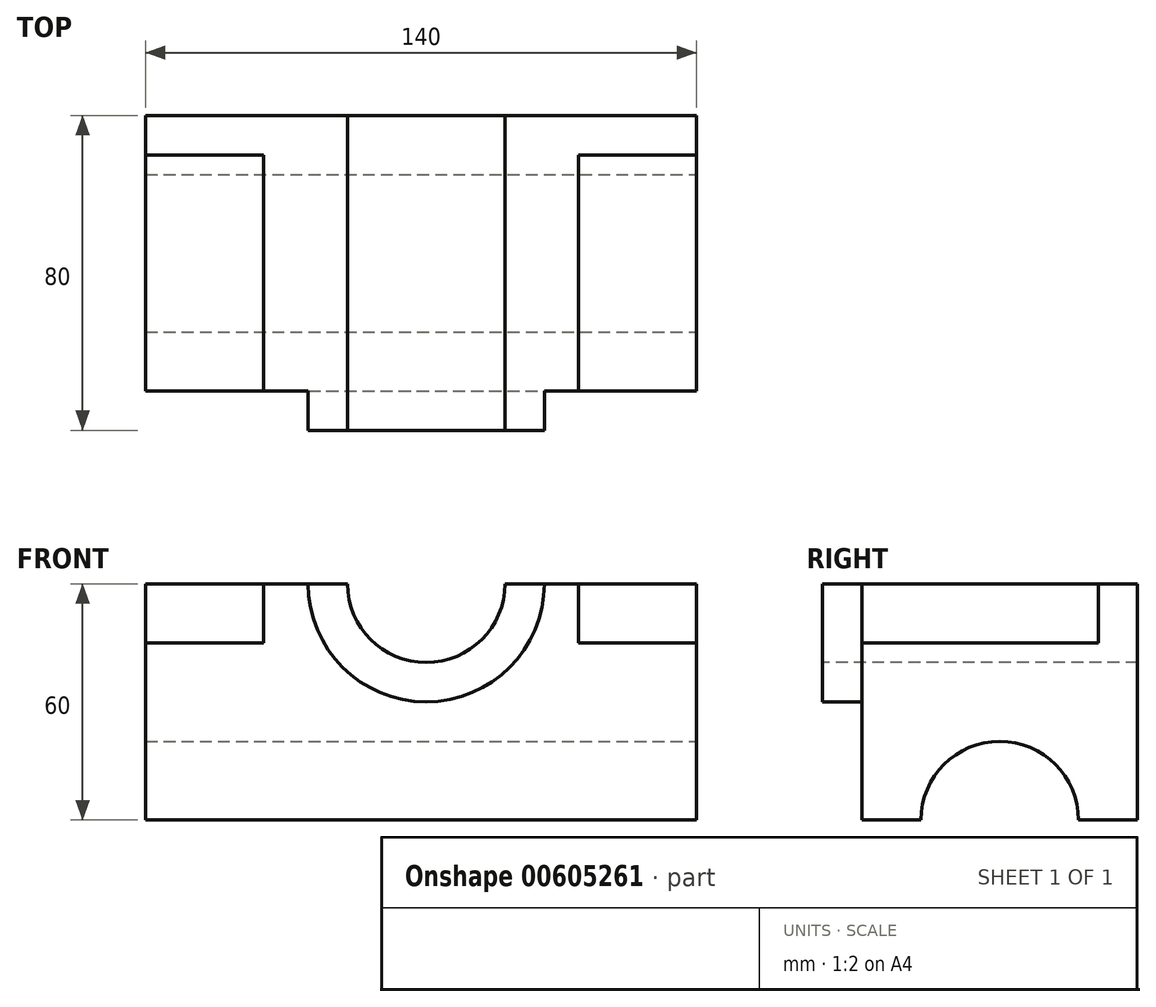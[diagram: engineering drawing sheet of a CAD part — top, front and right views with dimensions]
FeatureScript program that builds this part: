
annotation { "Feature Type Name" : "Feature", "Feature Type Description" : "" }
export const myFeature = defineFeature(function(context is Context, id is Id, definition is map)
    precondition{}
    {
        {
            var Q0;
            Q0=qCreatedBy(makeId("Top.planeOp"),FACE);
            var sketch = newSketch(context, id + "F0", { "sketchPlane" : qUnion([Q0])});
            skLineSegment(sketch, "E0.bottom", {"start": v(-71.28, 46.73) * mm, "end": v(68.72, 46.73) * mm});
            skLineSegment(sketch, "E0.top", {"start": v(-71.28, -23.27) * mm, "end": v(68.72, -23.27) * mm});
            skLineSegment(sketch, "E0.left", {"start": v(-71.28, 46.73) * mm, "end": v(-71.28, -23.27) * mm});
            skLineSegment(sketch, "E0.right", {"start": v(68.72, 46.73) * mm, "end": v(68.72, -23.27) * mm});
            skSolve(sketch);
        }
        {
            var Q0;
            Q0=makeQuery(id+"F0.imprint","IMPRINT",FACE,{"disambiguationData":[TD([[makeQuery(id+"F0.imprint","IMPRINT",EDGE,{"derivedFrom":sQuery(id+"F0.wireOp",EDGE,"E0.bottom")}),-1.0]])]});
            extrude(context, id + "F1", {"entities" : qUnion([Q0]), "depth" : 60 * mm, "offsetDistance" : 25 * mm});
        }
        {
            var Q0;
            Q0=makeQuery(id+"F1.opExtrude","SWEPT_FACE",FACE,{"disambiguationData":[OSD([sQuery(id+"F0.wireOp",EDGE,"E0.right")])]});
            var sketch = newSketch(context, id + "F2", { "sketchPlane" : qUnion([Q0])});
            skCircle(sketch, "E1", {"center": v(11.73, 0) * mm, "radius": 20 * mm});
            skSolve(sketch);
        }
        {
            var Q0;
            {var subQ0=sQuery(id+"F2.wireOp",EDGE,"E1");var subQ1=makeQuery(id+"F1.opExtrude","CAP_EDGE",EDGE,{"disambiguationData":[OSD([sQuery(id+"F0.wireOp",EDGE,"E0.right")])],"isStart":true});var subQ2=makeQuery(id+"F2.imprint","INTERSECT",VERTEX,{"disambiguationData":[OD(0.0)],"derivedFrom":[subQ1,subQ0]});Q0=makeQuery(id+"F2.imprint","IMPRINT",FACE,{"disambiguationData":[TD([[makeQuery(id+"F2.imprint","IMPRINT",EDGE,{"disambiguationData":[TD([[subQ2,-1.0]])],"derivedFrom":subQ0}),1.0]])]});}
            extrude(context, id + "F3", {"entities" : qUnion([Q0]), "operationType" : NewBodyOperationType.REMOVE, "oppositeDirection" : true, "depth" : 140 * mm, "offsetDistance" : 25 * mm});
        }
        {
            var Q0;
            Q0=makeQuery(id+"F1.opExtrude","SWEPT_FACE",FACE,{"disambiguationData":[OSD([sQuery(id+"F0.wireOp",EDGE,"E0.top")])]});
            var sketch = newSketch(context, id + "F4", { "sketchPlane" : qUnion([Q0])});
            skCircle(sketch, "E2", {"center": v(0, 60) * mm, "radius": 20 * mm});
            skCircle(sketch, "E3", {"center": v(0, 60) * mm, "radius": 30 * mm});
            skSolve(sketch);
        }
        {
            var Q0;
            {var subQ0=sQuery(id+"F4.wireOp",EDGE,"E2");var subQ1=makeQuery(id+"F1.opExtrude","CAP_EDGE",EDGE,{"disambiguationData":[OSD([sQuery(id+"F0.wireOp",EDGE,"E0.top")])],"isStart":false});var subQ2=makeQuery(id+"F4.imprint","INTERSECT",VERTEX,{"disambiguationData":[OD(0.0)],"derivedFrom":[subQ1,subQ0]});Q0=makeQuery(id+"F4.imprint","IMPRINT",FACE,{"disambiguationData":[TD([[makeQuery(id+"F4.imprint","IMPRINT",EDGE,{"disambiguationData":[TD([[subQ2,-1.0]])],"derivedFrom":subQ0}),1.0]])]});}
            extrude(context, id + "F5", {"entities" : qUnion([Q0]), "operationType" : NewBodyOperationType.REMOVE, "oppositeDirection" : true, "depth" : 70 * mm, "offsetDistance" : 25 * mm});
        }
        {
            var Q0;
            {var subQ0=sQuery(id+"F4.wireOp",EDGE,"E2");var subQ1=makeQuery(id+"F1.opExtrude","CAP_EDGE",EDGE,{"disambiguationData":[OSD([sQuery(id+"F0.wireOp",EDGE,"E0.top")])],"isStart":false});var subQ2=makeQuery(id+"F4.imprint","INTERSECT",VERTEX,{"disambiguationData":[OD(0.0)],"derivedFrom":[subQ1,subQ0]});Q0=makeQuery(id+"F4.imprint","IMPRINT",FACE,{"disambiguationData":[TD([[makeQuery(id+"F4.imprint","IMPRINT",EDGE,{"disambiguationData":[TD([[subQ2,-1.0]])],"derivedFrom":subQ0}),-1.0]])]});}
            extrude(context, id + "F6", {"entities" : qUnion([Q0]), "operationType" : NewBodyOperationType.ADD, "depth" : 10 * mm, "offsetDistance" : 25 * mm});
        }
        {
            var Q0;
            {var subQ0=sQuery(id+"F0.wireOp",EDGE,"E0.top");var subQ1=makeQuery(id+"F1.opExtrude","CAP_EDGE",EDGE,{"disambiguationData":[OSD([subQ0])],"isStart":false});var subQ3=sQuery(id+"F0.wireOp",EDGE,"E0.bottom");var subQ4=sQuery(id+"F0.wireOp",EDGE,"E0.left");Q0=makeQuery(id+"F6.boolean.opBoolean","MERGE",FACE,{"derivedFrom":[makeQuery(id+"F5.boolean.opBoolean","SPLIT",FACE,{"disambiguationData":[TD([makeQuery(id+"F1.opExtrude","SWEPT_FACE",FACE,{"disambiguationData":[OSD([subQ4])]})])],"derivedFrom":makeQuery(id+"F1.opExtrude","CAP_FACE",FACE,{"disambiguationData":[OSD([subQ3,subQ0,subQ4,sQuery(id+"F0.wireOp",EDGE,"E0.right")])],"isStart":false})}),makeQuery(id+"F6.opExtrude","SWEPT_FACE",FACE,{"disambiguationData":[OSD([subQ0]),TDD([makeQuery(id+"F4.imprint","IMPRINT",EDGE,{"disambiguationData":[TD([[makeQuery(id+"F4.imprint","INTERSECT",VERTEX,{"disambiguationData":[OD(0.0)],"derivedFrom":[subQ1,sQuery(id+"F4.wireOp",EDGE,"E3")]}),-1.0]])],"derivedFrom":subQ1})])]})]});}
            var sketch = newSketch(context, id + "F7", { "sketchPlane" : qUnion([Q0])});
            skLineSegment(sketch, "E4.bottom", {"start": v(-71.28, -23.27) * mm, "end": v(-41.28, -23.27) * mm});
            skLineSegment(sketch, "E4.top", {"start": v(-71.28, 36.73) * mm, "end": v(-41.28, 36.73) * mm});
            skLineSegment(sketch, "E4.left", {"start": v(-71.28, -23.27) * mm, "end": v(-71.28, 36.73) * mm});
            skLineSegment(sketch, "E4.right", {"start": v(-41.28, -23.27) * mm, "end": v(-41.28, 36.73) * mm});
            skSolve(sketch);
        }
        {
            var Q0;
            Q0=makeQuery(id+"F7.imprint","IMPRINT",FACE,{"disambiguationData":[TD([[makeQuery(id+"F7.imprint","IMPRINT",EDGE,{"derivedFrom":sQuery(id+"F7.wireOp",EDGE,"E4.bottom")}),1.0]])]});
            extrude(context, id + "F8", {"entities" : qUnion([Q0]), "operationType" : NewBodyOperationType.REMOVE, "oppositeDirection" : true, "depth" : 15 * mm, "offsetDistance" : 25 * mm});
        }
        {
            var Q0;
            {var subQ0=sQuery(id+"F0.wireOp",EDGE,"E0.top");var subQ1=makeQuery(id+"F1.opExtrude","CAP_EDGE",EDGE,{"disambiguationData":[OSD([subQ0])],"isStart":false});var subQ3=sQuery(id+"F0.wireOp",EDGE,"E0.bottom");var subQ4=sQuery(id+"F0.wireOp",EDGE,"E0.right");Q0=makeQuery(id+"F6.boolean.opBoolean","MERGE",FACE,{"derivedFrom":[makeQuery(id+"F5.boolean.opBoolean","SPLIT",FACE,{"disambiguationData":[TD([makeQuery(id+"F1.opExtrude","SWEPT_FACE",FACE,{"disambiguationData":[OSD([subQ4])]})])],"derivedFrom":makeQuery(id+"F1.opExtrude","CAP_FACE",FACE,{"disambiguationData":[OSD([subQ3,subQ0,sQuery(id+"F0.wireOp",EDGE,"E0.left"),subQ4])],"isStart":false})}),makeQuery(id+"F6.opExtrude","SWEPT_FACE",FACE,{"disambiguationData":[OSD([subQ0]),TDD([makeQuery(id+"F4.imprint","IMPRINT",EDGE,{"disambiguationData":[TD([[makeQuery(id+"F4.imprint","INTERSECT",VERTEX,{"disambiguationData":[OD(1.0)],"derivedFrom":[subQ1,sQuery(id+"F4.wireOp",EDGE,"E3")]}),1.0]])],"derivedFrom":subQ1})])]})]});}
            var sketch = newSketch(context, id + "F9", { "sketchPlane" : qUnion([Q0])});
            skLineSegment(sketch, "E5.bottom", {"start": v(68.72, -23.27) * mm, "end": v(38.72, -23.27) * mm});
            skLineSegment(sketch, "E5.top", {"start": v(68.72, 36.73) * mm, "end": v(38.72, 36.73) * mm});
            skLineSegment(sketch, "E5.left", {"start": v(68.72, -23.27) * mm, "end": v(68.72, 36.73) * mm});
            skLineSegment(sketch, "E5.right", {"start": v(38.72, -23.27) * mm, "end": v(38.72, 36.73) * mm});
            skSolve(sketch);
        }
        {
            var Q0;
            Q0=makeQuery(id+"F9.imprint","IMPRINT",FACE,{"disambiguationData":[TD([[makeQuery(id+"F9.imprint","IMPRINT",EDGE,{"derivedFrom":sQuery(id+"F9.wireOp",EDGE,"E5.bottom")}),1.0]])]});
            extrude(context, id + "F10", {"entities" : qUnion([Q0]), "operationType" : NewBodyOperationType.REMOVE, "oppositeDirection" : true, "depth" : 15 * mm, "offsetDistance" : 25 * mm});
        }
    });
